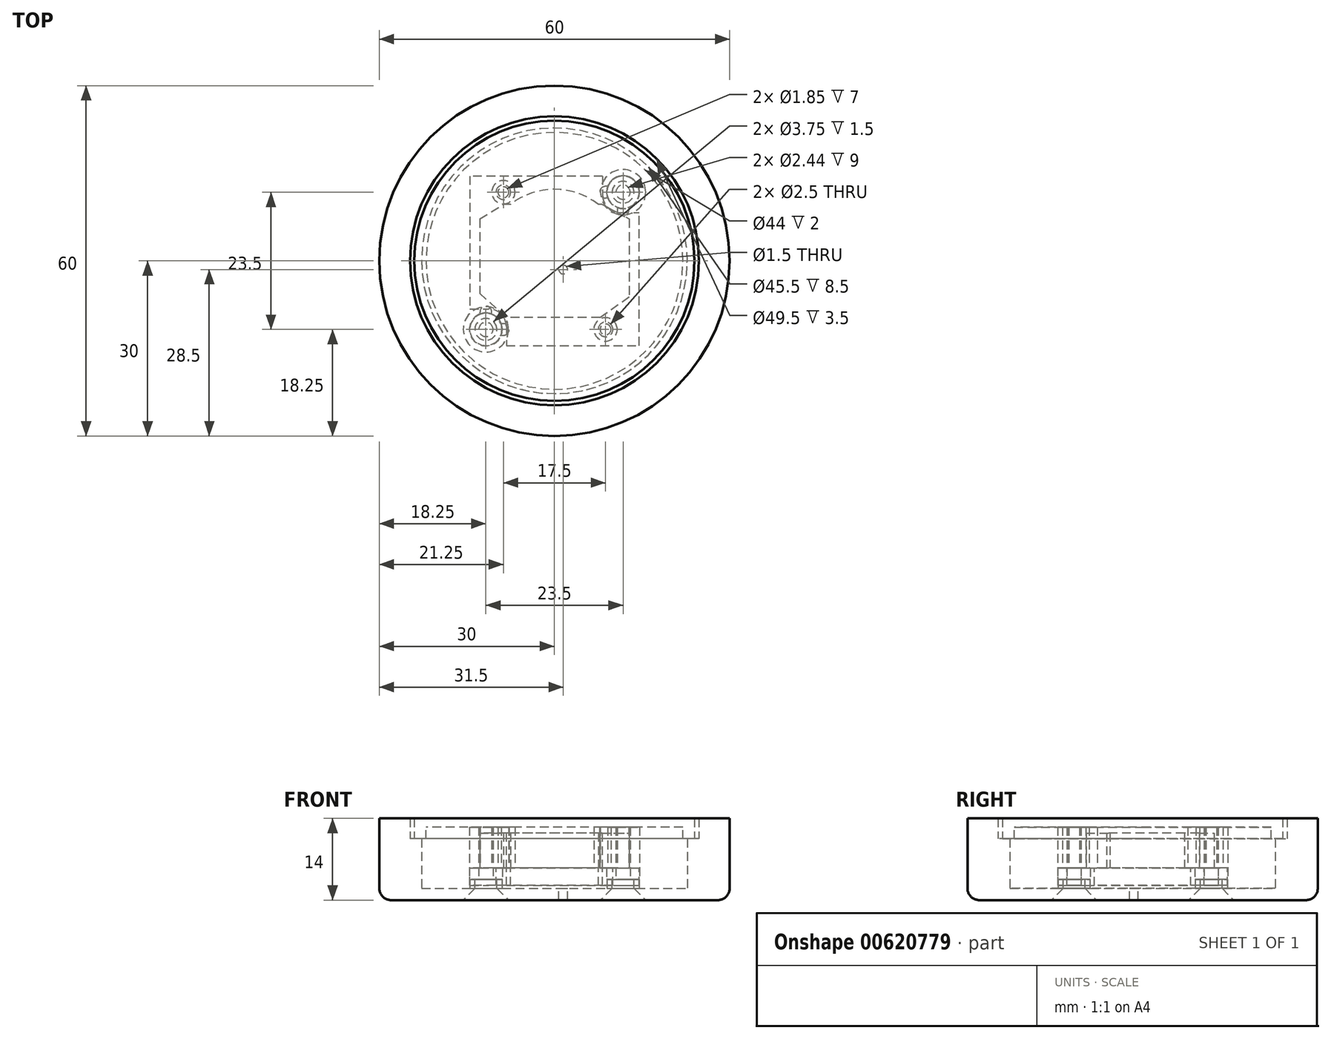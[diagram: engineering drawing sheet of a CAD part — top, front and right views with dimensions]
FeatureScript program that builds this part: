
annotation { "Feature Type Name" : "Feature", "Feature Type Description" : "" }
export const myFeature = defineFeature(function(context is Context, id is Id, definition is map)
    precondition{}
    {
        {
            var Q0;
            Q0=qCreatedBy(makeId("Top.planeOp"),FACE);
            var sketch = newSketch(context, id + "F0", { "sketchPlane" : qUnion([Q0])});
            skPoint(sketch, "E0.middle", {"position": v(0, 0) * mm});
            skCircle(sketch, "E1", {"center": v(-8.75, 11.75) * mm, "radius": 1.25 * mm});
            skLineSegment(sketch, "E2", {"start": v(8.25, 14.5) * mm, "end": v(8.25, 11.25) * mm});
            skLineSegment(sketch, "E3", {"start": v(11.25, 8.25) * mm, "end": v(14.5, 8.25) * mm});
            skLineSegment(sketch, "E4", {"start": v(8.25, 14.5) * mm, "end": v(-14.5, 14.5) * mm});
            skLineSegment(sketch, "E5", {"start": v(14.5, -14.5) * mm, "end": v(14.5, 8.25) * mm});
            skArc(sketch, "E6.filletArc", {"start": v(8.25, 11.25) * mm, "mid": v(9.13, 9.13) * mm, "end": v(11.25, 8.25) * mm});
            skLineSegment(sketch, "E7", {"start": v(-14.5, 14.5) * mm, "end": v(-14.5, -8.25) * mm});
            skLineSegment(sketch, "E8", {"start": v(-14.5, -8.25) * mm, "end": v(-11.25, -8.25) * mm});
            skLineSegment(sketch, "E9", {"start": v(-8.25, -11.25) * mm, "end": v(-8.25, -14.5) * mm});
            skLineSegment(sketch, "E10", {"start": v(-8.25, -14.5) * mm, "end": v(14.5, -14.5) * mm});
            skArc(sketch, "E11.filletArc", {"start": v(-8.25, -11.25) * mm, "mid": v(-9.13, -9.13) * mm, "end": v(-11.25, -8.25) * mm});
            skCircle(sketch, "E12", {"center": v(8.75, -11.75) * mm, "radius": 1.25 * mm});
            skSolve(sketch);
        }
        {
            var Q0;
            Q0=makeQuery(id+"F0.imprint","IMPRINT",FACE,{"disambiguationData":[TD([[makeQuery(id+"F0.imprint","IMPRINT",EDGE,{"derivedFrom":sQuery(id+"F0.wireOp",EDGE,"E1")}),-1.0]])]});
            extrude(context, id + "F1", {"entities" : qUnion([Q0]), "oppositeDirection" : true, "depth" : 3 * mm, "offsetDistance" : 25 * mm});
        }
        {
            var Q0;
            Q0=qCreatedBy(makeId("Top.planeOp"),FACE);
            var sketch = newSketch(context, id + "F2", { "sketchPlane" : qUnion([Q0])});
            skCircle(sketch, "E13", {"center": v(0, 0) * mm, "radius": 12.25 * mm});
            skLineSegment(sketch, "E14.bottom", {"start": v(12.8, 9.68) * mm, "end": v(-12.8, 9.68) * mm});
            skLineSegment(sketch, "E14.top", {"start": v(12.8, -9.68) * mm, "end": v(-12.8, -9.68) * mm});
            skLineSegment(sketch, "E14.left", {"start": v(12.8, 9.68) * mm, "end": v(12.8, -9.68) * mm});
            skLineSegment(sketch, "E14.right", {"start": v(-12.8, 9.68) * mm, "end": v(-12.8, -9.68) * mm});
            skLineSegment(sketch, "E15", {"start": v(8.17, 9.68) * mm, "end": v(12.8, 7.18) * mm});
            skLineSegment(sketch, "E16", {"start": v(7.8, -9.68) * mm, "end": v(12.8, -6.18) * mm});
            skLineSegment(sketch, "E17", {"start": v(-8.3, -9.68) * mm, "end": v(-12.8, -5.58) * mm});
            skLineSegment(sketch, "E18", {"start": v(-12.8, 7.18) * mm, "end": v(-8.71, 9.68) * mm});
            skSolve(sketch);
        }
        {
            var Q0;
            {var subQ0=sQuery(id+"F2.wireOp",EDGE,"E14.bottom");var subQ1=sQuery(id+"F2.wireOp",EDGE,"E13");var subQ2=makeQuery(id+"F2.imprint","INTERSECT",VERTEX,{"disambiguationData":[OD(0.0)],"derivedFrom":[subQ1,subQ0]});Q0=makeQuery(id+"F2.imprint","IMPRINT",FACE,{"disambiguationData":[TD([[makeQuery(id+"F2.imprint","IMPRINT",EDGE,{"disambiguationData":[TD([[subQ2,1.0]])],"derivedFrom":subQ1}),1.0]])]});}
            var Q1;
            {var subQ0=sQuery(id+"F2.wireOp",EDGE,"E14.top");var subQ1=sQuery(id+"F2.wireOp",EDGE,"E13");var subQ2=makeQuery(id+"F2.imprint","INTERSECT",VERTEX,{"disambiguationData":[OD(0.0)],"derivedFrom":[subQ1,subQ0]});Q1=makeQuery(id+"F2.imprint","IMPRINT",FACE,{"disambiguationData":[TD([[makeQuery(id+"F2.imprint","IMPRINT",EDGE,{"disambiguationData":[TD([[subQ2,-1.0]])],"derivedFrom":subQ1}),1.0]])]});}
            var Q2;
            {var subQ0=sQuery(id+"F2.wireOp",EDGE,"E17");Q2=makeQuery(id+"F2.imprint","IMPRINT",FACE,{"disambiguationData":[TD([[makeQuery(id+"F2.imprint","IMPRINT",EDGE,{"derivedFrom":subQ0}),-1.0]])]});}
            var Q3;
            {var subQ0=sQuery(id+"F2.wireOp",EDGE,"E15");Q3=makeQuery(id+"F2.imprint","IMPRINT",FACE,{"disambiguationData":[TD([[makeQuery(id+"F2.imprint","IMPRINT",EDGE,{"derivedFrom":subQ0}),-1.0]])]});}
            var Q4;
            {var subQ0=sQuery(id+"F2.wireOp",EDGE,"E14.bottom");var subQ1=sQuery(id+"F2.wireOp",EDGE,"E13");var subQ2=makeQuery(id+"F2.imprint","INTERSECT",VERTEX,{"disambiguationData":[OD(0.0)],"derivedFrom":[subQ1,subQ0]});Q4=makeQuery(id+"F2.imprint","IMPRINT",FACE,{"disambiguationData":[TD([[makeQuery(id+"F2.imprint","IMPRINT",EDGE,{"disambiguationData":[TD([[subQ2,-1.0]])],"derivedFrom":subQ1}),1.0]])]});}
            extrude(context, id + "F3", {"entities" : qUnion([Q0, Q1, Q2, Q3, Q4]), "operationType" : NewBodyOperationType.ADD, "depth" : 6 * mm, "offsetDistance" : 25 * mm});
        }
        {
            var Q0;
            Q0=qCreatedBy(makeId("Top.planeOp"),FACE);
            var sketch = newSketch(context, id + "F4", { "sketchPlane" : qUnion([Q0])});
            skCircle(sketch, "E19", {"center": v(-11.75, -11.75) * mm, "radius": 1.22 * mm});
            skCircle(sketch, "E20", {"center": v(11.75, 11.75) * mm, "radius": 1.22 * mm});
            skCircle(sketch, "E21", {"center": v(11.75, 11.75) * mm, "radius": 2.81 * mm});
            skCircle(sketch, "E22", {"center": v(-11.75, -11.75) * mm, "radius": 2.81 * mm});
            skLineSegment(sketch, "E23", {"start": v(-8.94, -8.94) * mm, "end": v(8.94, -8.94) * mm, "construction": true});
            skLineSegment(sketch, "E24", {"start": v(8.94, 8.94) * mm, "end": v(-8.94, 8.94) * mm, "construction": true});
            skLineSegment(sketch, "E25", {"start": v(8.94, -8.94) * mm, "end": v(8.94, 8.94) * mm, "construction": true});
            skLineSegment(sketch, "E26", {"start": v(-8.94, 8.94) * mm, "end": v(-8.94, -8.94) * mm, "construction": true});
            skPoint(sketch, "E27", {"position": v(-8.94, 0) * mm});
            skPoint(sketch, "E28", {"position": v(0, 8.94) * mm});
            skPoint(sketch, "E29", {"position": v(8.75, -11.75) * mm});
            skCircle(sketch, "E30", {"center": v(-8.75, 11.75) * mm, "radius": 2 * mm});
            skCircle(sketch, "E31", {"center": v(8.75, -11.75) * mm, "radius": 2 * mm});
            skCircle(sketch, "E32", {"center": v(-8.75, 11.75) * mm, "radius": 0.93 * mm});
            skCircle(sketch, "E33", {"center": v(8.75, -11.75) * mm, "radius": 0.93 * mm});
            skLineSegment(sketch, "E34", {"start": v(-11.75, -11.75) * mm, "end": v(-11.75, -7.75) * mm, "construction": true});
            skLineSegment(sketch, "E35", {"start": v(-8.94, 8.94) * mm, "end": v(8.94, -8.94) * mm, "construction": true});
            skLineSegment(sketch, "E36", {"start": v(-11.75, -7.75) * mm, "end": v(-11.75, -7.75) * mm});
            skLineSegment(sketch, "E37", {"start": v(-12.75, -9.12) * mm, "end": v(-12.75, -8.75) * mm});
            skPoint(sketch, "E38.visualSharp", {"position": v(-12.75, -7.75) * mm});
            skArc(sketch, "E38.filletArc", {"start": v(-11.75, -7.75) * mm, "mid": v(-12.46, -8.04) * mm, "end": v(-12.75, -8.75) * mm});
            skArc(sketch, "E39.MirrorCS", {"start": v(-11.75, -7.75) * mm, "mid": v(-11.04, -8.04) * mm, "end": v(-10.75, -8.75) * mm});
            skLineSegment(sketch, "E40.MirrorCS", {"start": v(-10.75, -9.12) * mm, "end": v(-10.75, -8.75) * mm});
            skLineSegment(sketch, "E41", {"start": v(8.94, 8.94) * mm, "end": v(-8.94, -8.94) * mm, "construction": true});
            skLineSegment(sketch, "E42.MirrorCS", {"start": v(-9.12, -12.75) * mm, "end": v(-8.75, -12.75) * mm});
            skArc(sketch, "E43.MirrorCS", {"start": v(-7.75, -11.75) * mm, "mid": v(-8.04, -12.46) * mm, "end": v(-8.75, -12.75) * mm});
            skArc(sketch, "E44.MirrorCS", {"start": v(-7.75, -11.75) * mm, "mid": v(-8.04, -11.04) * mm, "end": v(-8.75, -10.75) * mm});
            skLineSegment(sketch, "E45.MirrorCS", {"start": v(-9.12, -10.75) * mm, "end": v(-8.75, -10.75) * mm});
            skLineSegment(sketch, "E46.MirrorCS", {"start": v(10.75, 9.12) * mm, "end": v(10.75, 8.75) * mm});
            skArc(sketch, "E47.MirrorCS", {"start": v(11.75, 7.75) * mm, "mid": v(11.04, 8.04) * mm, "end": v(10.75, 8.75) * mm});
            skArc(sketch, "E48.MirrorCS", {"start": v(11.75, 7.75) * mm, "mid": v(12.46, 8.04) * mm, "end": v(12.75, 8.75) * mm});
            skLineSegment(sketch, "E49.MirrorCS", {"start": v(12.75, 9.12) * mm, "end": v(12.75, 8.75) * mm});
            skLineSegment(sketch, "E50.MirrorCS", {"start": v(9.12, 10.75) * mm, "end": v(8.75, 10.75) * mm});
            skArc(sketch, "E51.MirrorCS", {"start": v(7.75, 11.75) * mm, "mid": v(8.04, 11.04) * mm, "end": v(8.75, 10.75) * mm});
            skArc(sketch, "E52.MirrorCS", {"start": v(7.75, 11.75) * mm, "mid": v(8.04, 12.46) * mm, "end": v(8.75, 12.75) * mm});
            skLineSegment(sketch, "E53.MirrorCS", {"start": v(9.12, 12.75) * mm, "end": v(8.75, 12.75) * mm});
            skCircle(sketch, "E54", {"center": v(0, 0) * mm, "radius": 30 * mm, "construction": true});
            skCircle(sketch, "E55", {"center": v(1.5, -1.5) * mm, "radius": 0.75 * mm});
            skLineSegment(sketch, "E56", {"start": v(-11.75, -11.75) * mm, "end": v(1.5, -1.5) * mm, "construction": true});
            skLineSegment(sketch, "E57", {"start": v(-8.75, 11.75) * mm, "end": v(1.5, -1.5) * mm, "construction": true});
            skSolve(sketch);
        }
        {
            var Q0;
            Q0=makeQuery(id+"F4.imprint","IMPRINT",FACE,{"disambiguationData":[TD([[makeQuery(id+"F4.imprint","IMPRINT",EDGE,{"derivedFrom":sQuery(id+"F4.wireOp",EDGE,"E19")}),-1.0]])]});
            var Q1;
            Q1=makeQuery(id+"F4.imprint","IMPRINT",FACE,{"disambiguationData":[TD([[makeQuery(id+"F4.imprint","IMPRINT",EDGE,{"derivedFrom":sQuery(id+"F4.wireOp",EDGE,"E31")}),1.0]])]});
            var Q2;
            {var subQ0=sQuery(id+"F4.wireOp",EDGE,"E42.MirrorCS");Q2=makeQuery(id+"F4.imprint","IMPRINT",FACE,{"disambiguationData":[TD([[makeQuery(id+"F4.imprint","IMPRINT",EDGE,{"derivedFrom":subQ0}),1.0]])]});}
            var Q3;
            {var subQ0=sQuery(id+"F4.wireOp",EDGE,"E50.MirrorCS");Q3=makeQuery(id+"F4.imprint","IMPRINT",FACE,{"disambiguationData":[TD([[makeQuery(id+"F4.imprint","IMPRINT",EDGE,{"derivedFrom":subQ0}),-1.0]])]});}
            var Q4;
            {var subQ0=sQuery(id+"F4.wireOp",EDGE,"E46.MirrorCS");Q4=makeQuery(id+"F4.imprint","IMPRINT",FACE,{"disambiguationData":[TD([[makeQuery(id+"F4.imprint","IMPRINT",EDGE,{"derivedFrom":subQ0}),1.0]])]});}
            var Q5;
            Q5=makeQuery(id+"F4.imprint","IMPRINT",FACE,{"disambiguationData":[TD([[makeQuery(id+"F4.imprint","IMPRINT",EDGE,{"derivedFrom":sQuery(id+"F4.wireOp",EDGE,"E20")}),-1.0]])]});
            var Q6;
            Q6=makeQuery(id+"F4.imprint","IMPRINT",FACE,{"disambiguationData":[TD([[makeQuery(id+"F4.imprint","IMPRINT",EDGE,{"derivedFrom":sQuery(id+"F4.wireOp",EDGE,"E30")}),1.0]])]});
            var Q7;
            {var subQ0=sQuery(id+"F4.wireOp",EDGE,"E37");Q7=makeQuery(id+"F4.imprint","IMPRINT",FACE,{"disambiguationData":[TD([[makeQuery(id+"F4.imprint","IMPRINT",EDGE,{"derivedFrom":subQ0}),-1.0]])]});}
            extrude(context, id + "F5", {"entities" : qUnion([Q0, Q1, Q2, Q3, Q4, Q5, Q6, Q7]), "depth" : 7 * mm, "offsetDistance" : 25 * mm});
        }
        {
            var Q0;
            Q0=makeQuery(id+"F5.opExtrude","CAP_FACE",FACE,{"disambiguationData":[OSD([sQuery(id+"F4.wireOp",EDGE,"E19"),sQuery(id+"F4.wireOp",EDGE,"E22"),sQuery(id+"F4.wireOp",EDGE,"E37"),sQuery(id+"F4.wireOp",EDGE,"E38.filletArc"),sQuery(id+"F4.wireOp",EDGE,"E39.MirrorCS"),sQuery(id+"F4.wireOp",EDGE,"E40.MirrorCS"),sQuery(id+"F4.wireOp",EDGE,"E42.MirrorCS"),sQuery(id+"F4.wireOp",EDGE,"E43.MirrorCS"),sQuery(id+"F4.wireOp",EDGE,"E44.MirrorCS"),sQuery(id+"F4.wireOp",EDGE,"E45.MirrorCS")])],"isStart":false});
            cPlane(context, id + "F6", {"entities" : qUnion([Q0]), "cplaneType" : CPlaneType.OFFSET, "offset" : 0 * mm, "width" : 150 * mm, "height" : 150 * mm});
        }
        {
            var Q0;
            Q0=qCreatedBy(id+"F6.planeOp",FACE);
            var sketch = newSketch(context, id + "F7", { "sketchPlane" : qUnion([Q0])});
            skPoint(sketch, "E58", {"position": v(0, 0) * mm});
            skCircle(sketch, "E59", {"center": v(0, 0) * mm, "radius": 24 * mm});
            skCircle(sketch, "E60", {"center": v(0, 0) * mm, "radius": 21 * mm});
            skCircle(sketch, "E61", {"center": v(0, 0) * mm, "radius": 22 * mm});
            skSolve(sketch);
        }
        {
            var Q0;
            Q0 = qSketchRegion(id + "F7", true);
            var Q1;
            Q1=makeQuery(id+"F7.imprint","IMPRINT",FACE,{"disambiguationData":[TD([[makeQuery(id+"F7.imprint","IMPRINT",EDGE,{"derivedFrom":sQuery(id+"F7.wireOp",EDGE,"E60")}),1.0]])]});
            var Q2;
            Q2=makeQuery(id+"F7.imprint","IMPRINT",FACE,{"disambiguationData":[TD([[makeQuery(id+"F7.imprint","IMPRINT",EDGE,{"derivedFrom":sQuery(id+"F7.wireOp",EDGE,"E60")}),-1.0]])]});
            extrude(context, id + "F8", {"entities" : qUnion([Q0, Q1, Q2]), "operationType" : NewBodyOperationType.ADD, "depth" : 1.5 * mm, "offsetDistance" : 25 * mm});
        }
        {
            var Q0;
            Q0=makeQuery(id+"F4.imprint","IMPRINT",FACE,{"disambiguationData":[TD([[makeQuery(id+"F4.imprint","IMPRINT",EDGE,{"derivedFrom":sQuery(id+"F4.wireOp",EDGE,"E19")}),-1.0]])]});
            var Q1;
            Q1=makeQuery(id+"F4.imprint","IMPRINT",FACE,{"disambiguationData":[TD([[makeQuery(id+"F4.imprint","IMPRINT",EDGE,{"derivedFrom":sQuery(id+"F4.wireOp",EDGE,"E20")}),-1.0]])]});
            extrude(context, id + "F9", {"entities" : qUnion([Q0, Q1]), "operationType" : NewBodyOperationType.ADD, "oppositeDirection" : true, "depth" : 2 * mm, "offsetDistance" : 25 * mm});
        }
        {
            var Q0;
            Q0=makeQuery(id+"F7.imprint","IMPRINT",FACE,{"disambiguationData":[TD([[makeQuery(id+"F7.imprint","IMPRINT",EDGE,{"derivedFrom":sQuery(id+"F7.wireOp",EDGE,"E59")}),1.0]])]});
            extrude(context, id + "F10", {"entities" : qUnion([Q0]), "operationType" : NewBodyOperationType.ADD, "oppositeDirection" : true, "depth" : 2 * mm, "offsetDistance" : 25 * mm});
        }
        {
            var Q0;
            Q0=makeQuery(id+"F1.opExtrude","CAP_FACE",FACE,{"disambiguationData":[OSD([sQuery(id+"F0.wireOp",EDGE,"E1"),sQuery(id+"F0.wireOp",EDGE,"E2"),sQuery(id+"F0.wireOp",EDGE,"E3"),sQuery(id+"F0.wireOp",EDGE,"E4"),sQuery(id+"F0.wireOp",EDGE,"E5"),sQuery(id+"F0.wireOp",EDGE,"E6.filletArc"),sQuery(id+"F0.wireOp",EDGE,"E7"),sQuery(id+"F0.wireOp",EDGE,"E8"),sQuery(id+"F0.wireOp",EDGE,"E9"),sQuery(id+"F0.wireOp",EDGE,"E10"),sQuery(id+"F0.wireOp",EDGE,"E11.filletArc"),sQuery(id+"F0.wireOp",EDGE,"E12")])],"isStart":false});
            cPlane(context, id + "F11", {"entities" : qUnion([Q0]), "cplaneType" : CPlaneType.OFFSET, "offset" : 0.5 * mm, "width" : 150 * mm, "height" : 150 * mm});
        }
        {
            var Q0;
            Q0=qCreatedBy(id+"F11.planeOp",FACE);
            var sketch = newSketch(context, id + "F12", { "sketchPlane" : qUnion([Q0])});
            skPoint(sketch, "E62", {"position": v(-11.75, 11.75) * mm});
            skPoint(sketch, "E63", {"position": v(0, 0) * mm});
            skPoint(sketch, "E64", {"position": v(11.75, -11.75) * mm});
            skCircle(sketch, "E65", {"center": v(-11.75, 11.75) * mm, "radius": 1.88 * mm});
            skCircle(sketch, "E66", {"center": v(-11.75, 11.75) * mm, "radius": 2.75 * mm});
            skCircle(sketch, "E67", {"center": v(11.75, -11.75) * mm, "radius": 1.88 * mm});
            skCircle(sketch, "E68", {"center": v(11.75, -11.75) * mm, "radius": 2.75 * mm});
            skPoint(sketch, "E69", {"position": v(1.5, 1.5) * mm});
            skCircle(sketch, "E70", {"center": v(1.5, 1.5) * mm, "radius": 0.75 * mm});
            skCircle(sketch, "E71", {"center": v(0, 0) * mm, "radius": 24 * mm, "construction": true});
            skCircle(sketch, "E72", {"center": v(0, 0) * mm, "radius": 22.75 * mm});
            skCircle(sketch, "E73", {"center": v(0, 0) * mm, "radius": 24.75 * mm});
            skCircle(sketch, "E74", {"center": v(0, 0) * mm, "radius": 30 * mm});
            skSolve(sketch);
        }
        {
            var Q0;
            Q0=makeQuery(id+"F12.imprint","IMPRINT",FACE,{"disambiguationData":[TD([[makeQuery(id+"F12.imprint","IMPRINT",EDGE,{"derivedFrom":sQuery(id+"F12.wireOp",EDGE,"E73")}),-1.0]])]});
            var Q1;
            Q1=makeQuery(id+"F12.imprint","IMPRINT",FACE,{"disambiguationData":[TD([[makeQuery(id+"F12.imprint","IMPRINT",EDGE,{"derivedFrom":sQuery(id+"F12.wireOp",EDGE,"E72")}),-1.0]])]});
            var Q2;
            Q2=makeQuery(id+"F12.imprint","IMPRINT",FACE,{"disambiguationData":[TD([[makeQuery(id+"F12.imprint","IMPRINT",EDGE,{"derivedFrom":sQuery(id+"F12.wireOp",EDGE,"E66")}),-1.0]])]});
            var Q3;
            Q3=makeQuery(id+"F12.imprint","IMPRINT",FACE,{"disambiguationData":[TD([[makeQuery(id+"F12.imprint","IMPRINT",EDGE,{"derivedFrom":sQuery(id+"F12.wireOp",EDGE,"E65")}),-1.0]])]});
            var Q4;
            Q4=makeQuery(id+"F12.imprint","IMPRINT",FACE,{"disambiguationData":[TD([[makeQuery(id+"F12.imprint","IMPRINT",EDGE,{"derivedFrom":sQuery(id+"F12.wireOp",EDGE,"E67")}),-1.0]])]});
            extrude(context, id + "F13", {"entities" : qUnion([Q0, Q1, Q2, Q3, Q4]), "depth" : 2 * mm, "offsetDistance" : 25 * mm});
        }
        {
            var Q0;
            Q0=makeQuery(id+"F12.imprint","IMPRINT",FACE,{"disambiguationData":[TD([[makeQuery(id+"F12.imprint","IMPRINT",EDGE,{"derivedFrom":sQuery(id+"F12.wireOp",EDGE,"E67")}),-1.0]])]});
            var Q1;
            Q1=makeQuery(id+"F12.imprint","IMPRINT",FACE,{"disambiguationData":[TD([[makeQuery(id+"F12.imprint","IMPRINT",EDGE,{"derivedFrom":sQuery(id+"F12.wireOp",EDGE,"E65")}),-1.0]])]});
            extrude(context, id + "F14", {"entities" : qUnion([Q0, Q1]), "operationType" : NewBodyOperationType.ADD, "oppositeDirection" : true, "depth" : 1.5 * mm, "offsetDistance" : 25 * mm});
        }
        {
            var Q0;
            Q0=makeQuery(id+"F13.opExtrude","CAP_EDGE",EDGE,{"disambiguationData":[OSD([sQuery(id+"F12.wireOp",EDGE,"E65")])],"isStart":false});
            var Q1;
            Q1=makeQuery(id+"F13.opExtrude","CAP_EDGE",EDGE,{"disambiguationData":[OSD([sQuery(id+"F12.wireOp",EDGE,"E67")])],"isStart":false});
            chamfer(context, id + "F15", {"entities" : qUnion([Q0, Q1]), "width" : 2 * mm, "tangentPropagation" : true});
        }
        {
            var Q0;
            Q0=makeQuery(id+"F12.imprint","IMPRINT",FACE,{"disambiguationData":[TD([[makeQuery(id+"F12.imprint","IMPRINT",EDGE,{"derivedFrom":sQuery(id+"F12.wireOp",EDGE,"E72")}),-1.0]])]});
            var Q1;
            Q1=makeQuery(id+"F10.opExtrude","CAP_FACE",FACE,{"disambiguationData":[OSD([sQuery(id+"F7.wireOp",EDGE,"E59"),sQuery(id+"F7.wireOp",EDGE,"E61")])],"isStart":false});
            extrude(context, id + "F16", {"entities" : qUnion([Q0]), "operationType" : NewBodyOperationType.ADD, "endBound" : BoundingType.UP_TO_SURFACE, "oppositeDirection" : true, "depth" : 25 * mm, "endBoundEntityFace" : qUnion([Q1]), "offsetDistance" : 25 * mm});
        }
        {
            var Q0;
            Q0=makeQuery(id+"F12.imprint","IMPRINT",FACE,{"disambiguationData":[TD([[makeQuery(id+"F12.imprint","IMPRINT",EDGE,{"derivedFrom":sQuery(id+"F12.wireOp",EDGE,"E73")}),-1.0]])]});
            extrude(context, id + "F17", {"entities" : qUnion([Q0]), "operationType" : NewBodyOperationType.ADD, "oppositeDirection" : true, "depth" : 12 * mm, "offsetDistance" : 25 * mm});
        }
        {
            var Q0;
            Q0=makeQuery(id+"F13.opExtrude","CAP_EDGE",EDGE,{"disambiguationData":[OSD([sQuery(id+"F12.wireOp",EDGE,"E74")])],"isStart":false});
            fillet(context, id + "F18", {"entities" : qUnion([Q0]), "radius" : 2 * mm, "tangentPropagation" : true, "allowEdgeOverflow" : false});
        }
    });
